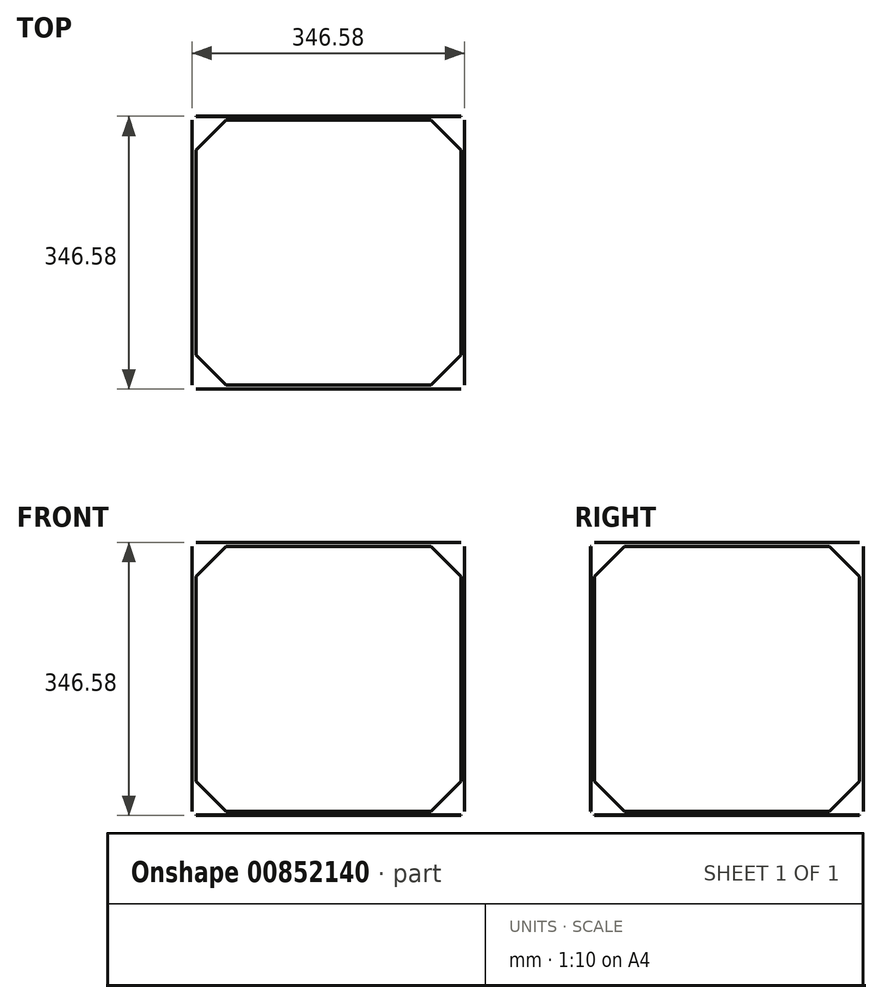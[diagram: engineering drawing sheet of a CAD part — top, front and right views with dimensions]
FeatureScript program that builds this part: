
annotation { "Feature Type Name" : "Feature", "Feature Type Description" : "" }
export const myFeature = defineFeature(function(context is Context, id is Id, definition is map)
    precondition{}
    {
        {
            var Q0;
            Q0=qCreatedBy(makeId("Front.planeOp"),FACE);
            var sketch = newSketch(context, id + "F0", { "sketchPlane" : qUnion([Q0])});
            skLineSegment(sketch, "E0.bottom", {"start": v(0, 0) * mm, "end": v(355.6, 0) * mm});
            skLineSegment(sketch, "E0.top", {"start": v(0, 355.6) * mm, "end": v(355.6, 355.6) * mm});
            skLineSegment(sketch, "E0.left", {"start": v(0, 0) * mm, "end": v(0, 355.6) * mm});
            skLineSegment(sketch, "E0.right", {"start": v(355.6, 0) * mm, "end": v(355.6, 355.6) * mm});
            skLineSegment(sketch, "E1", {"start": v(177.8, 0) * mm, "end": v(177.8, -32.05) * mm});
            skLineSegment(sketch, "E2", {"start": v(0, 177.8) * mm, "end": v(-57.86, 177.8) * mm});
            skSolve(sketch);
        }
        {
            var Q0;
            Q0=qCreatedBy(makeId("Front.planeOp"),FACE);
            cPlane(context, id + "F1", {"entities" : qUnion([Q0]), "cplaneType" : CPlaneType.OFFSET, "offset" : 4.76 * mm, "oppositeDirection" : true, "width" : 152.4 * mm, "height" : 152.4 * mm});
        }
        {
            var Q0;
            Q0=qCreatedBy(id+"F1.planeOp",FACE);
            var sketch = newSketch(context, id + "F2", { "sketchPlane" : qUnion([Q0])});
            skLineSegment(sketch, "E3.0", {"start": v(9.52, 15.88) * mm, "end": v(9.52, 339.72) * mm});
            skLineSegment(sketch, "E4.0", {"start": v(15.88, 346.08) * mm, "end": v(339.72, 346.08) * mm});
            skLineSegment(sketch, "E5.0", {"start": v(346.08, 15.88) * mm, "end": v(346.07, 339.72) * mm});
            skLineSegment(sketch, "E6.0", {"start": v(15.88, 9.52) * mm, "end": v(339.72, 9.52) * mm});
            skLineSegment(sketch, "E7", {"start": v(47.62, 9.53) * mm, "end": v(9.53, 47.62) * mm});
            skLineSegment(sketch, "E8.MirrorCS", {"start": v(47.63, 346.08) * mm, "end": v(9.52, 307.98) * mm});
            skLineSegment(sketch, "E9.MirrorCS", {"start": v(307.98, 9.52) * mm, "end": v(346.08, 47.63) * mm});
            skLineSegment(sketch, "E10.MirrorCS", {"start": v(307.98, 346.08) * mm, "end": v(346.08, 307.98) * mm});
            skPoint(sketch, "E11.visualSharp", {"position": v(9.52, 346.08) * mm});
            skArc(sketch, "E11.filletArc", {"start": v(15.88, 346.08) * mm, "mid": v(11.38, 344.22) * mm, "end": v(9.52, 339.72) * mm});
            skPoint(sketch, "E12.visualSharp", {"position": v(346.07, 346.08) * mm});
            skArc(sketch, "E12.filletArc", {"start": v(346.08, 339.72) * mm, "mid": v(344.22, 344.22) * mm, "end": v(339.72, 346.08) * mm});
            skPoint(sketch, "E13.visualSharp", {"position": v(346.08, 9.53) * mm});
            skArc(sketch, "E13.filletArc", {"start": v(339.72, 9.53) * mm, "mid": v(344.22, 11.38) * mm, "end": v(346.07, 15.88) * mm});
            skPoint(sketch, "E14.visualSharp", {"position": v(9.52, 9.53) * mm});
            skArc(sketch, "E14.filletArc", {"start": v(9.52, 15.88) * mm, "mid": v(11.38, 11.38) * mm, "end": v(15.88, 9.53) * mm});
            skSolve(sketch);
        }
        {
            var Q0;
            Q0=qCreatedBy(makeId("Top.planeOp"),FACE);
            cPlane(context, id + "F3", {"entities" : qUnion([Q0]), "cplaneType" : CPlaneType.OFFSET, "offset" : 25.4 * mm, "width" : 152.4 * mm, "height" : 152.4 * mm});
        }
        {
            var Q0;
            Q0=qCreatedBy(id+"F3.planeOp",FACE);
            var sketch = newSketch(context, id + "F4", { "sketchPlane" : qUnion([Q0])});
            skCircle(sketch, "E15", {"center": v(9.53, 4.76) * mm, "radius": 1.59 * mm});
            skSolve(sketch);
        }
        {
            var Q0;
            Q0=qCreatedBy(makeId("Right.planeOp"),FACE);
            var Q1;
            Q1=qCreatedBy(makeId("Front.planeOp"),FACE);
            cPlane(context, id + "F5", {"entities" : qUnion([Q0, Q1]), "cplaneType" : CPlaneType.MID_PLANE, "offset" : 25.4 * mm, "flipAlignment" : true, "width" : 152.4 * mm, "height" : 152.4 * mm});
        }
        {
            var Q0;
            {var subQ0=sQuery(id+"F2.wireOp",EDGE,"E7");Q0=makeQuery(id+"F2.imprint","IMPRINT",FACE,{"disambiguationData":[TD([[makeQuery(id+"F2.imprint","IMPRINT",EDGE,{"derivedFrom":subQ0}),-1.0]])]});}
            var Q1;
            Q1=sQuery(id+"F2.wireOp",EDGE,"E8.MirrorCS");
            extrude(context, id + "F6", {"entities" : qUnion([Q0]), "surfaceOperationType" : NewSurfaceOperationType.ADD, "surfaceEntities" : qUnion([Q1]), "depth" : 0.25 * mm, "offsetDistance" : 25.4 * mm});
        }
        {
            var Q0;
            Q0=makeQuery(id+"F6.opExtrude","SWEPT_BODY",BODY,{"disambiguationData":[OSD([sQuery(id+"F2.wireOp",EDGE,"E3.0"),sQuery(id+"F2.wireOp",EDGE,"E4.0"),sQuery(id+"F2.wireOp",EDGE,"E5.0"),sQuery(id+"F2.wireOp",EDGE,"E6.0"),sQuery(id+"F2.wireOp",EDGE,"E7"),sQuery(id+"F2.wireOp",EDGE,"E8.MirrorCS"),sQuery(id+"F2.wireOp",EDGE,"E9.MirrorCS"),sQuery(id+"F2.wireOp",EDGE,"E10.MirrorCS")])]});
            var Q1;
            Q1=makeQuery(id+"Ffpau8pWhRCDQo4_0.opSweep","SWEPT_BODY",BODY,{"disambiguationData":[OSD([sQuery(id+"F2.wireOp",EDGE,"E14.filletArc"),sQuery(id+"F4.wireOp",EDGE,"E15")])]});
            var Q2;
            Q2=qCreatedBy(id+"F5.planeOp",FACE);
            mirror(context, id + "F7", {"entities" : qUnion([Q0, Q1]), "mirrorPlane" : qUnion([Q2])});
        }
        {
            var Q0;
            Q0=qCreatedBy(makeId("Front.planeOp"),FACE);
            cPlane(context, id + "F8", {"entities" : qUnion([Q0]), "cplaneType" : CPlaneType.OFFSET, "offset" : 177.8 * mm, "oppositeDirection" : true, "width" : 152.4 * mm, "height" : 152.4 * mm});
        }
        {
            var Q0;
            Q0=makeQuery(id+"F6.opExtrude","SWEPT_BODY",BODY,{"disambiguationData":[OSD([sQuery(id+"F2.wireOp",EDGE,"E3.0"),sQuery(id+"F2.wireOp",EDGE,"E4.0"),sQuery(id+"F2.wireOp",EDGE,"E5.0"),sQuery(id+"F2.wireOp",EDGE,"E6.0"),sQuery(id+"F2.wireOp",EDGE,"E7"),sQuery(id+"F2.wireOp",EDGE,"E8.MirrorCS"),sQuery(id+"F2.wireOp",EDGE,"E9.MirrorCS"),sQuery(id+"F2.wireOp",EDGE,"E10.MirrorCS")])]});
            var Q1;
            Q1=makeQuery(id+"Ffpau8pWhRCDQo4_0.opSweep","SWEPT_BODY",BODY,{"disambiguationData":[OSD([sQuery(id+"F2.wireOp",EDGE,"E14.filletArc"),sQuery(id+"F4.wireOp",EDGE,"E15")])]});
            var Q2;
            Q2=qCreatedBy(id+"F8.planeOp",FACE);
            mirror(context, id + "F9", {"entities" : qUnion([Q0, Q1]), "mirrorPlane" : qUnion([Q2])});
        }
        {
            var Q0;
            Q0=qCreatedBy(makeId("Right.planeOp"),FACE);
            cPlane(context, id + "F10", {"entities" : qUnion([Q0]), "cplaneType" : CPlaneType.OFFSET, "offset" : 177.8 * mm, "width" : 152.4 * mm, "height" : 152.4 * mm});
        }
        {
            var Q0;
            Q0=makeQuery(id+"F7.opPattern","COPY",BODY,{"derivedFrom":makeQuery(id+"F6.opExtrude","SWEPT_BODY",BODY,{"disambiguationData":[OSD([sQuery(id+"F2.wireOp",EDGE,"E3.0"),sQuery(id+"F2.wireOp",EDGE,"E4.0"),sQuery(id+"F2.wireOp",EDGE,"E5.0"),sQuery(id+"F2.wireOp",EDGE,"E6.0"),sQuery(id+"F2.wireOp",EDGE,"E7"),sQuery(id+"F2.wireOp",EDGE,"E8.MirrorCS"),sQuery(id+"F2.wireOp",EDGE,"E9.MirrorCS"),sQuery(id+"F2.wireOp",EDGE,"E10.MirrorCS")])]}),"instanceName":"1"});
            var Q1;
            Q1=makeQuery(id+"F7.opPattern","COPY",BODY,{"derivedFrom":makeQuery(id+"Ffpau8pWhRCDQo4_0.opSweep","SWEPT_BODY",BODY,{"disambiguationData":[OSD([sQuery(id+"F2.wireOp",EDGE,"E14.filletArc"),sQuery(id+"F4.wireOp",EDGE,"E15")])]}),"instanceName":"1"});
            var Q2;
            Q2=qCreatedBy(id+"F10.planeOp",FACE);
            mirror(context, id + "F11", {"entities" : qUnion([Q0, Q1]), "mirrorPlane" : qUnion([Q2])});
        }
        {
            var Q0;
            Q0=qCreatedBy(makeId("Top.planeOp"),FACE);
            var Q1;
            Q1=qCreatedBy(makeId("Right.planeOp"),FACE);
            cPlane(context, id + "F12", {"entities" : qUnion([Q0, Q1]), "cplaneType" : CPlaneType.MID_PLANE, "offset" : 25.4 * mm, "width" : 152.4 * mm, "height" : 152.4 * mm});
        }
        {
            var Q0;
            Q0=makeQuery(id+"F7.opPattern","COPY",BODY,{"derivedFrom":makeQuery(id+"Ffpau8pWhRCDQo4_0.opSweep","SWEPT_BODY",BODY,{"disambiguationData":[OSD([sQuery(id+"F2.wireOp",EDGE,"E14.filletArc"),sQuery(id+"F4.wireOp",EDGE,"E15")])]}),"instanceName":"1"});
            var Q1;
            Q1=makeQuery(id+"F7.opPattern","COPY",BODY,{"derivedFrom":makeQuery(id+"F6.opExtrude","SWEPT_BODY",BODY,{"disambiguationData":[OSD([sQuery(id+"F2.wireOp",EDGE,"E3.0"),sQuery(id+"F2.wireOp",EDGE,"E4.0"),sQuery(id+"F2.wireOp",EDGE,"E5.0"),sQuery(id+"F2.wireOp",EDGE,"E6.0"),sQuery(id+"F2.wireOp",EDGE,"E7"),sQuery(id+"F2.wireOp",EDGE,"E8.MirrorCS"),sQuery(id+"F2.wireOp",EDGE,"E9.MirrorCS"),sQuery(id+"F2.wireOp",EDGE,"E10.MirrorCS")])]}),"instanceName":"1"});
            var Q2;
            Q2=qCreatedBy(id+"F12.planeOp",FACE);
            mirror(context, id + "F13", {"entities" : qUnion([Q0, Q1]), "mirrorPlane" : qUnion([Q2])});
        }
        {
            var Q0;
            Q0=qCreatedBy(makeId("Top.planeOp"),FACE);
            cPlane(context, id + "F14", {"entities" : qUnion([Q0]), "cplaneType" : CPlaneType.OFFSET, "offset" : 177.8 * mm, "width" : 152.4 * mm, "height" : 152.4 * mm});
        }
        {
            var Q0;
            Q0=makeQuery(id+"F13.opPattern","COPY",BODY,{"derivedFrom":makeQuery(id+"F7.opPattern","COPY",BODY,{"derivedFrom":makeQuery(id+"Ffpau8pWhRCDQo4_0.opSweep","SWEPT_BODY",BODY,{"disambiguationData":[OSD([sQuery(id+"F2.wireOp",EDGE,"E14.filletArc"),sQuery(id+"F4.wireOp",EDGE,"E15")])]}),"instanceName":"1"}),"instanceName":"1"});
            var Q1;
            Q1=makeQuery(id+"F13.opPattern","COPY",BODY,{"derivedFrom":makeQuery(id+"F7.opPattern","COPY",BODY,{"derivedFrom":makeQuery(id+"F6.opExtrude","SWEPT_BODY",BODY,{"disambiguationData":[OSD([sQuery(id+"F2.wireOp",EDGE,"E3.0"),sQuery(id+"F2.wireOp",EDGE,"E4.0"),sQuery(id+"F2.wireOp",EDGE,"E5.0"),sQuery(id+"F2.wireOp",EDGE,"E6.0"),sQuery(id+"F2.wireOp",EDGE,"E7"),sQuery(id+"F2.wireOp",EDGE,"E8.MirrorCS"),sQuery(id+"F2.wireOp",EDGE,"E9.MirrorCS"),sQuery(id+"F2.wireOp",EDGE,"E10.MirrorCS")])]}),"instanceName":"1"}),"instanceName":"1"});
            var Q2;
            Q2=qCreatedBy(id+"F14.planeOp",FACE);
            mirror(context, id + "F15", {"entities" : qUnion([Q0, Q1]), "mirrorPlane" : qUnion([Q2])});
        }
    });
